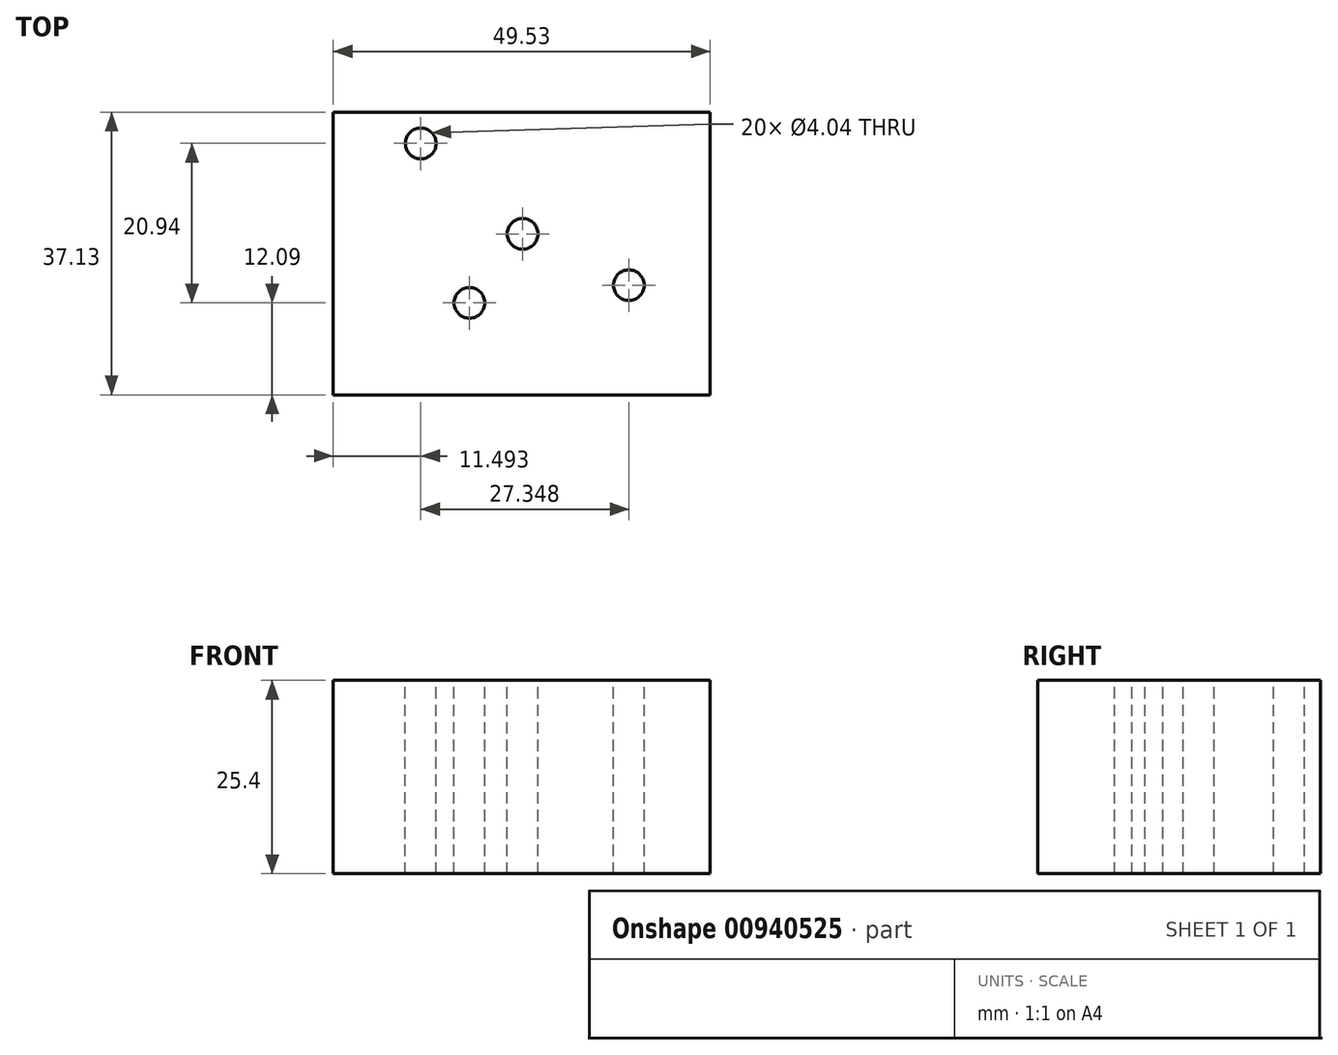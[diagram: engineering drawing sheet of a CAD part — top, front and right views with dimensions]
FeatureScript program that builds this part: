
annotation { "Feature Type Name" : "Feature", "Feature Type Description" : "" }
export const myFeature = defineFeature(function(context is Context, id is Id, definition is map)
    precondition{}
    {
        {
            var Q0;
            Q0=qCreatedBy(makeId("Top.planeOp"),FACE);
            var sketch = newSketch(context, id + "F0", { "sketchPlane" : qUnion([Q0])});
            skLineSegment(sketch, "E0.bottom", {"start": v(-24.88, -12.09) * mm, "end": v(24.65, -12.09) * mm});
            skLineSegment(sketch, "E0.top", {"start": v(-24.88, 25.04) * mm, "end": v(24.65, 25.04) * mm});
            skLineSegment(sketch, "E0.left", {"start": v(-24.88, -12.09) * mm, "end": v(-24.88, 25.04) * mm});
            skLineSegment(sketch, "E0.right", {"start": v(24.65, -12.09) * mm, "end": v(24.65, 25.04) * mm});
            skSolve(sketch);
        }
        {
            var Q0;
            Q0 = qSketchRegion(id + "F0", true);
            extrude(context, id + "F1", {"entities" : qUnion([Q0]), "depth" : 25.4 * mm, "offsetDistance" : 25.4 * mm});
        }
        {
            var Q0;
            Q0=makeQuery(id+"F1.opExtrude","CAP_FACE",FACE,{"disambiguationData":[OSD([sQuery(id+"F0.wireOp",EDGE,"E0.bottom"),sQuery(id+"F0.wireOp",EDGE,"E0.top"),sQuery(id+"F0.wireOp",EDGE,"E0.left"),sQuery(id+"F0.wireOp",EDGE,"E0.right")])],"isStart":false});
            var sketch = newSketch(context, id + "F2", { "sketchPlane" : qUnion([Q0])});
            skPoint(sketch, "E1", {"position": v(-13.39, 20.94) * mm});
            skPoint(sketch, "E2", {"position": v(13.96, 2.31) * mm});
            skPoint(sketch, "E3", {"position": v(-6.98, 0) * mm});
            skPoint(sketch, "E4", {"position": v(0, 9.06) * mm});
            skSolve(sketch);
        }
        {
            var Q0;
            Q0=sQuery(id+"F2.wireOp",VERTEX,"E2");
            var Q1;
            Q1=sQuery(id+"F2.wireOp",VERTEX,"E1");
            var Q2;
            Q2=sQuery(id+"F2.wireOp",VERTEX,"E3");
            var Q3;
            Q3=sQuery(id+"F2.wireOp",VERTEX,"E4");
            var Q4;
            Q4=makeQuery(id+"F1.opExtrude","SWEPT_BODY",BODY,{"disambiguationData":[OSD([sQuery(id+"F0.wireOp",EDGE,"E0.bottom"),sQuery(id+"F0.wireOp",EDGE,"E0.top"),sQuery(id+"F0.wireOp",EDGE,"E0.left"),sQuery(id+"F0.wireOp",EDGE,"E0.right")])]});
            hole(context, id + "F3", {"style" : HoleStyle.SIMPLE, "endStyle" : HoleEndStyle.THROUGH, "standardTappedOrClearance" : lookupTablePath({ "standard" : "ANSI", "fit" : "Normal (ASME)", "engagement" : "75%", "pitch" : "32 tpi", "size" : "#10", "type" : "Tapped" }), "standardBlindInLast" : lookupTablePath({ "fit" : "Normal", "standard" : "ANSI", "engagement" : "75%", "pitch" : "32 tpi", "size" : "#10", "type" : "Clearance & tapped" }), "holeDiameter" : 4.04 * mm, "majorDiameter" : 4.83 * mm, "showTappedDepth" : true, "isTappedThrough" : true, "tappedDepth" : 12.7 * mm, "tapClearance" : 3, "locations" : qUnion([Q0, Q1, Q2, Q3]), "scope" : qUnion([Q4])});
        }
    });
